# Revit family: Haworth_BuzziBooth_Rib
name_source: partatom
category: Furniture
revit_build: Autodesk Revit Architecture 2015 (Build: 20141119_1515(x64)
units: mm (PartAtom-declared; Revit-internal decimal feet)

## types (2) — shared parameters
Actual Depth = 47 61/256"
Actual Width = 50 101/128"
Assembly Code = E2020200
Manufacturer = Haworth
Model = HCBZ-BHB
Revision Number = 1
Size = Verify Final Dim. w/ Haworth
URL = http://www.haworth.com
URL - Product = https://www.haworth.com
Warranty = http://www.haworth.com

## per-type parameters (varying)
| type | Actual Height | Description | Front Height | Single Booth | Standing Booth | Void Length |
| HCBZ-BHB2 | 92 33/256" | Haworth BuzziBooth - Standing Booth - 3D Rib | 83 59/128" | No | Yes | 14 71/128" |
| HCBZ-BHB1 | 85 5/128" | Haworth BuzziBooth - Single Booth - 3D Rib | 74 205/256" | Yes | No | 23 7/256" |

## geometry (parser evidence)
native form markers: Blend x11, Sweep x8
no freeform markers — native parametric forms only
